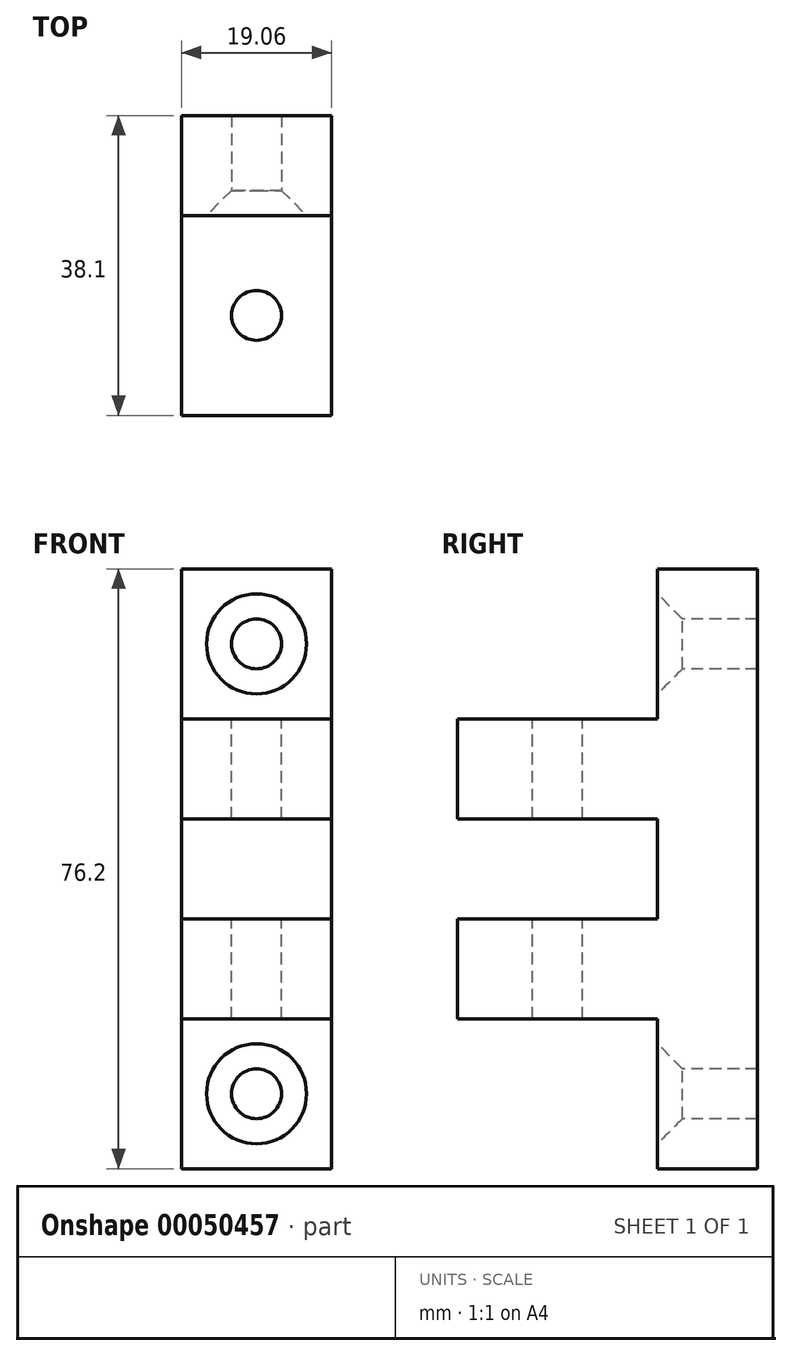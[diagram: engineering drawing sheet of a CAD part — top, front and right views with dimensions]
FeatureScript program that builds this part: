
annotation { "Feature Type Name" : "Feature", "Feature Type Description" : "" }
export const myFeature = defineFeature(function(context is Context, id is Id, definition is map)
    precondition{}
    {
        {
            var Q0;
            Q0=qCreatedBy(makeId("Front.planeOp"),FACE);
            var sketch = newSketch(context, id + "F0", { "sketchPlane" : qUnion([Q0])});
            skLineSegment(sketch, "E0.rect.bottom", {"start": v(9.53, 38.1) * mm, "end": v(-9.52, 38.1) * mm});
            skLineSegment(sketch, "E0.rect.top", {"start": v(9.52, -38.1) * mm, "end": v(-9.53, -38.1) * mm});
            skLineSegment(sketch, "E0.rect.left", {"start": v(9.53, 38.1) * mm, "end": v(9.52, -38.1) * mm});
            skLineSegment(sketch, "E0.rect.right", {"start": v(-9.52, 38.1) * mm, "end": v(-9.53, -38.1) * mm});
            skPoint(sketch, "E0.rect.middle", {"position": v(0, 0) * mm});
            skSolve(sketch);
        }
        {
            var Q0;
            Q0 = qSketchRegion(id + "F0", true);
            extrude(context, id + "F1", {"entities" : qUnion([Q0]), "depth" : 12.7 * mm});
        }
        {
            var Q0;
            Q0=makeQuery(id+"F1.opExtrude","CAP_FACE",FACE,{"disambiguationData":[OSD([sQuery(id+"F0.wireOp",EDGE,"E0.rect.bottom"),sQuery(id+"F0.wireOp",EDGE,"E0.rect.top"),sQuery(id+"F0.wireOp",EDGE,"E0.rect.left"),sQuery(id+"F0.wireOp",EDGE,"E0.rect.right")])],"isStart":false});
            var sketch = newSketch(context, id + "F2", { "sketchPlane" : qUnion([Q0])});
            skLineSegment(sketch, "E1.bottom", {"start": v(-9.52, 38.1) * mm, "end": v(9.53, 38.1) * mm});
            skLineSegment(sketch, "E1.top", {"start": v(-9.52, 19.05) * mm, "end": v(9.53, 19.05) * mm});
            skLineSegment(sketch, "E1.left", {"start": v(-9.52, 38.1) * mm, "end": v(-9.52, 19.05) * mm});
            skLineSegment(sketch, "E1.right", {"start": v(9.53, 38.1) * mm, "end": v(9.53, 19.05) * mm});
            skLineSegment(sketch, "E2.bottom", {"start": v(-9.53, -38.1) * mm, "end": v(9.52, -38.1) * mm});
            skLineSegment(sketch, "E2.top", {"start": v(-9.53, -19.05) * mm, "end": v(9.52, -19.05) * mm});
            skLineSegment(sketch, "E2.left", {"start": v(-9.53, -38.1) * mm, "end": v(-9.53, -19.05) * mm});
            skLineSegment(sketch, "E2.right", {"start": v(9.52, -38.1) * mm, "end": v(9.52, -19.05) * mm});
            skLineSegment(sketch, "E3.bottom", {"start": v(-9.53, 6.35) * mm, "end": v(9.53, 6.35) * mm});
            skLineSegment(sketch, "E3.top", {"start": v(-9.53, -6.35) * mm, "end": v(9.53, -6.35) * mm});
            skLineSegment(sketch, "E3.left", {"start": v(-9.53, 6.35) * mm, "end": v(-9.53, -6.35) * mm});
            skLineSegment(sketch, "E3.right", {"start": v(9.53, 6.35) * mm, "end": v(9.53, -6.35) * mm});
            skSolve(sketch);
        }
        {
            var Q0;
            {var subQ0=sQuery(id+"F2.wireOp",EDGE,"E2.top");Q0=makeQuery(id+"F2.imprint","IMPRINT",FACE,{"disambiguationData":[TD([[makeQuery(id+"F2.imprint","IMPRINT",EDGE,{"derivedFrom":subQ0}),1.0]])]});}
            var Q1;
            {var subQ0=sQuery(id+"F2.wireOp",EDGE,"E1.top");Q1=makeQuery(id+"F2.imprint","IMPRINT",FACE,{"disambiguationData":[TD([[makeQuery(id+"F2.imprint","IMPRINT",EDGE,{"derivedFrom":subQ0}),-1.0]])]});}
            extrude(context, id + "F3", {"entities" : qUnion([Q0, Q1]), "operationType" : NewBodyOperationType.ADD, "depth" : 25.4 * mm});
        }
        {
            var Q0;
            Q0=makeQuery(id+"F3.opExtrude","SWEPT_FACE",FACE,{"disambiguationData":[OSD([sQuery(id+"F2.wireOp",EDGE,"E1.top")])]});
            var sketch = newSketch(context, id + "F4", { "sketchPlane" : qUnion([Q0])});
            skPoint(sketch, "E4", {"position": v(0, -25.4) * mm});
            skSolve(sketch);
        }
        {
            var Q0;
            Q0=sQuery(id+"F4.wireOp",VERTEX,"E4");
            var Q1;
            Q1=makeQuery(id+"F1.opExtrude","SWEPT_BODY",BODY,{"disambiguationData":[OSD([sQuery(id+"F0.wireOp",EDGE,"E0.rect.bottom"),sQuery(id+"F0.wireOp",EDGE,"E0.rect.top"),sQuery(id+"F0.wireOp",EDGE,"E0.rect.left"),sQuery(id+"F0.wireOp",EDGE,"E0.rect.right")])]});
            hole(context, id + "F5", {"style" : HoleStyle.SIMPLE, "holeDiameter" : 6.35 * mm, "endStyle" : HoleEndStyle.THROUGH, "locations" : qUnion([Q0]), "scope" : qUnion([Q1])});
        }
        {
            var Q0;
            {var subQ0=sQuery(id+"F0.wireOp",EDGE,"E0.rect.right");var subQ6=sQuery(id+"F0.wireOp",EDGE,"E0.rect.left");var subQ7=sQuery(id+"F0.wireOp",EDGE,"E0.rect.bottom");Q0=makeQuery(id+"F3.boolean.opBoolean","SPLIT",FACE,{"disambiguationData":[TD([makeQuery(id+"F1.opExtrude","SWEPT_FACE",FACE,{"disambiguationData":[OSD([subQ7])]})])],"derivedFrom":makeQuery(id+"F1.opExtrude","CAP_FACE",FACE,{"disambiguationData":[OSD([subQ7,sQuery(id+"F0.wireOp",EDGE,"E0.rect.top"),subQ6,subQ0])],"isStart":false})});}
            var sketch = newSketch(context, id + "F6", { "sketchPlane" : qUnion([Q0])});
            skPoint(sketch, "E5", {"position": v(0, 28.57) * mm});
            skPoint(sketch, "E6.MirrorP", {"position": v(0, -28.57) * mm});
            skSolve(sketch);
        }
        {
            var Q0;
            Q0=sQuery(id+"F6.wireOp",VERTEX,"E5");
            var Q1;
            Q1=sQuery(id+"F6.wireOp",VERTEX,"E6.MirrorP");
            var Q2;
            Q2=makeQuery(id+"F1.opExtrude","SWEPT_BODY",BODY,{"disambiguationData":[OSD([sQuery(id+"F0.wireOp",EDGE,"E0.rect.bottom"),sQuery(id+"F0.wireOp",EDGE,"E0.rect.top"),sQuery(id+"F0.wireOp",EDGE,"E0.rect.left"),sQuery(id+"F0.wireOp",EDGE,"E0.rect.right")])]});
            hole(context, id + "F7", {"style" : HoleStyle.C_SINK, "holeDiameter" : 6.35 * mm, "cSinkDiameter" : 12.7 * mm, "endStyle" : HoleEndStyle.THROUGH, "locations" : qUnion([Q0, Q1]), "scope" : qUnion([Q2]), "cSinkAngle" : 90 * degree});
        }
    });
